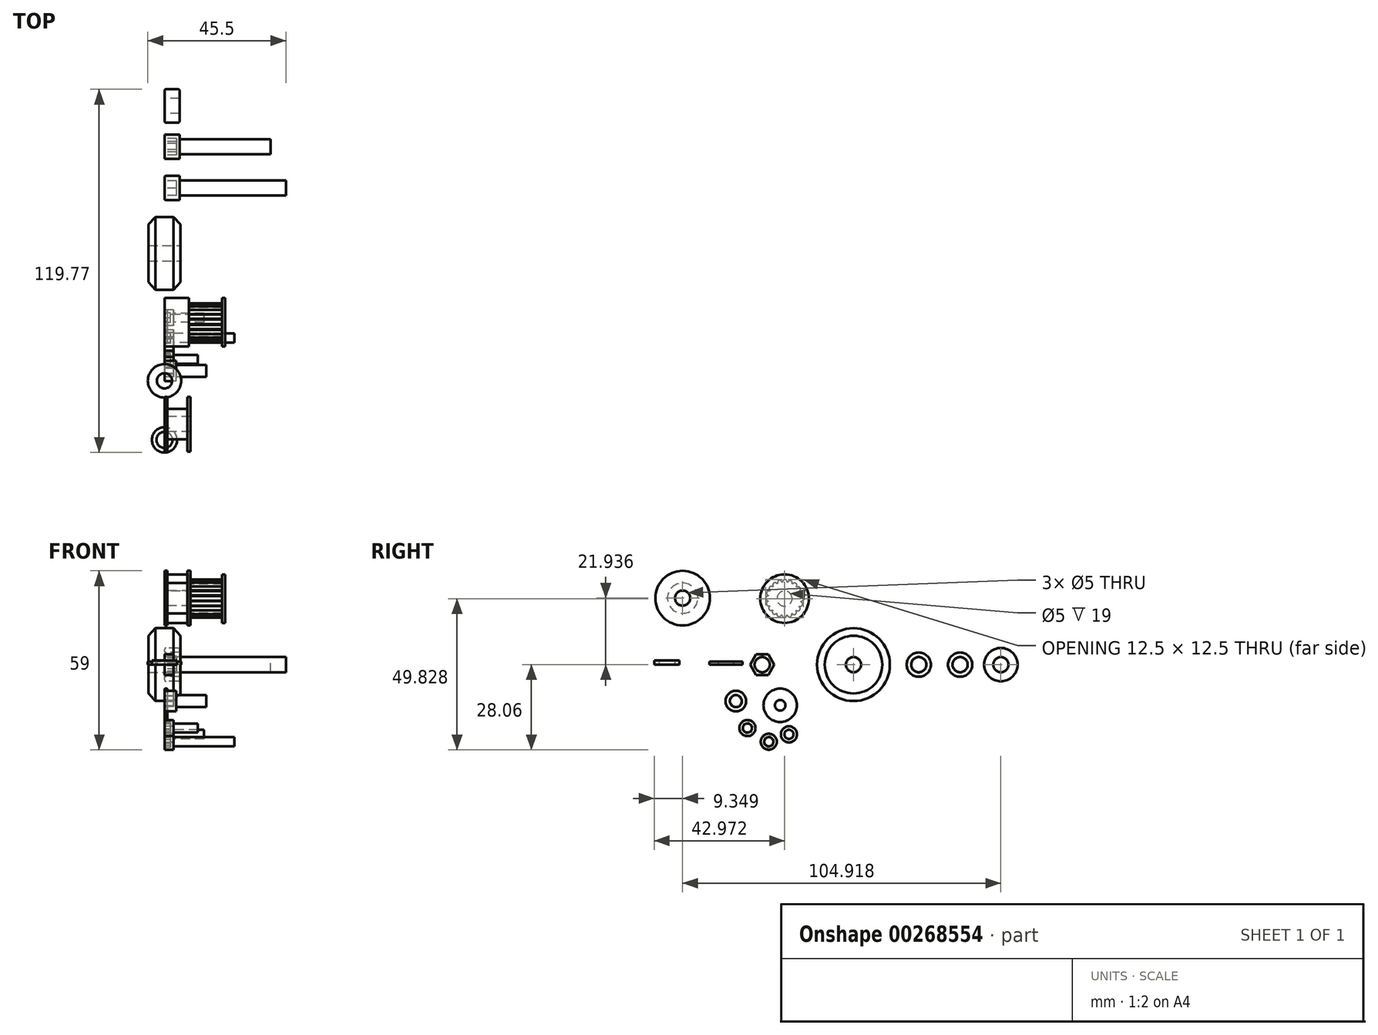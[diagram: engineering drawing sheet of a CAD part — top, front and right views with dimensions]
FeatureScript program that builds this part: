
annotation { "Feature Type Name" : "Feature", "Feature Type Description" : "" }
export const myFeature = defineFeature(function(context is Context, id is Id, definition is map)
    precondition{}
    {
        {
            var Q0;
            Q0=qCreatedBy(makeId("Top.planeOp"),FACE);
            var sketch = newSketch(context, id + "F0", { "sketchPlane" : qUnion([Q0])});
            skLineSegment(sketch, "E0", {"start": v(0, 12) * mm, "end": v(3, 12) * mm});
            skLineSegment(sketch, "E1", {"start": v(3, 12) * mm, "end": v(5.25, 9.5) * mm});
            skLineSegment(sketch, "E2", {"start": v(5.25, 9.5) * mm, "end": v(5.25, 2.5) * mm});
            skPoint(sketch, "E3.end.orphan", {"position": v(2.76, 0) * mm});
            skLineSegment(sketch, "E4", {"start": v(5.25, 2.5) * mm, "end": v(0, 2.5) * mm});
            skLineSegment(sketch, "E5", {"start": v(0, 2.5) * mm, "end": v(0, 12) * mm});
            skLineSegment(sketch, "E6.MirrorCS", {"start": v(0, 12) * mm, "end": v(-3, 12) * mm});
            skLineSegment(sketch, "E7.MirrorCS", {"start": v(-3, 12) * mm, "end": v(-5.25, 9.5) * mm});
            skLineSegment(sketch, "E8.MirrorCS", {"start": v(-5.25, 9.5) * mm, "end": v(-5.25, 2.5) * mm});
            skLineSegment(sketch, "E9.MirrorCS", {"start": v(-5.25, 2.5) * mm, "end": v(0, 2.5) * mm});
            skSolve(sketch);
        }
        {
            var Q0;
            Q0=qCreatedBy(makeId("Front.planeOp"),FACE);
            var sketch = newSketch(context, id + "F1", { "sketchPlane" : qUnion([Q0])});
            skLineSegment(sketch, "E10", {"start": v(9.9, 0) * mm, "end": v(-12.3, 0) * mm, "construction": true});
            skSolve(sketch);
        }
        {
            var Q0;
            Q0 = qSketchRegion(id + "F0", true);
            var Q1;
            Q1=sQuery(id+"F1.wireOp",EDGE,"E10");
            revolve(context, id + "F2", {"entities" : qUnion([Q0]), "axis" : qUnion([Q1]), "revolveType" : RevolveType.FULL});
        }
        {
            var Q0;
            Q0=qCreatedBy(makeId("Right.planeOp"),FACE);
            var sketch = newSketch(context, id + "F3", { "sketchPlane" : qUnion([Q0])});
            skCircle(sketch, "E11", {"center": v(35.14, 0) * mm, "radius": 4 * mm});
            skSolve(sketch);
        }
        {
            var Q0;
            Q0=makeQuery(id+"F3.imprint","IMPRINT",FACE,{"disambiguationData":[TD([[makeQuery(id+"F3.imprint","IMPRINT",EDGE,{"derivedFrom":sQuery(id+"F3.wireOp",EDGE,"E11")}),1.0]])]});
            var Q1;
            Q1=sQuery(id+"F3.wireOp",EDGE,"E11");
            extrude(context, id + "F4", {"entities" : qUnion([Q0]), "surfaceEntities" : qUnion([Q1]), "depth" : 5 * mm});
        }
        {
            var Q0;
            Q0=makeQuery(id+"F4.opExtrude","CAP_FACE",FACE,{"disambiguationData":[OSD([sQuery(id+"F3.wireOp",EDGE,"E11")])],"isStart":false});
            var sketch = newSketch(context, id + "F5", { "sketchPlane" : qUnion([Q0])});
            skCircle(sketch, "E12", {"center": v(35.14, 0) * mm, "radius": 2.5 * mm});
            skSolve(sketch);
        }
        {
            var Q0;
            Q0=makeQuery(id+"F5.imprint","IMPRINT",FACE,{"disambiguationData":[TD([[makeQuery(id+"F5.imprint","IMPRINT",EDGE,{"derivedFrom":sQuery(id+"F5.wireOp",EDGE,"E12")}),1.0]])]});
            extrude(context, id + "F6", {"entities" : qUnion([Q0]), "operationType" : NewBodyOperationType.ADD, "depth" : 30 * mm});
        }
        {
            var Q0;
            Q0=makeQuery(id+"F4.opExtrude","CAP_FACE",FACE,{"disambiguationData":[OSD([sQuery(id+"F3.wireOp",EDGE,"E11")])],"isStart":true});
            var sketch = newSketch(context, id + "F7", { "sketchPlane" : qUnion([Q0])});
            skCircle(sketch, "E13.cCircle", {"center": v(-35.14, 0) * mm, "radius": 2.76 * mm, "construction": true});
            skLineSegment(sketch, "E13.0", {"start": v(-34.13, -2.56) * mm, "end": v(-36.86, -2.16) * mm});
            skLineSegment(sketch, "E13.1", {"start": v(-36.86, -2.16) * mm, "end": v(-37.87, 0.4) * mm});
            skLineSegment(sketch, "E13.2", {"start": v(-37.87, 0.4) * mm, "end": v(-36.16, 2.56) * mm});
            skLineSegment(sketch, "E13.3", {"start": v(-36.16, 2.56) * mm, "end": v(-33.43, 2.16) * mm});
            skLineSegment(sketch, "E13.4", {"start": v(-33.43, 2.16) * mm, "end": v(-32.42, -0.4) * mm});
            skLineSegment(sketch, "E13.5", {"start": v(-32.42, -0.4) * mm, "end": v(-34.13, -2.56) * mm});
            skSolve(sketch);
        }
        {
            var Q0;
            Q0=makeQuery(id+"F7.imprint","IMPRINT",FACE,{"disambiguationData":[TD([[makeQuery(id+"F7.imprint","IMPRINT",EDGE,{"derivedFrom":sQuery(id+"F7.wireOp",EDGE,"E13.0")}),-1.0]])]});
            extrude(context, id + "F8", {"entities" : qUnion([Q0]), "operationType" : NewBodyOperationType.REMOVE, "oppositeDirection" : true, "depth" : 4 * mm});
        }
        {
            var Q0;
            Q0=qCreatedBy(makeId("Right.planeOp"),FACE);
            var sketch = newSketch(context, id + "F9", { "sketchPlane" : qUnion([Q0])});
            skCircle(sketch, "E14", {"center": v(48.59, 0) * mm, "radius": 5.5 * mm});
            skCircle(sketch, "E15", {"center": v(48.59, 0) * mm, "radius": 2.5 * mm});
            skSolve(sketch);
        }
        {
            var Q0;
            Q0 = qSketchRegion(id + "F9", true);
            extrude(context, id + "F10", {"entities" : qUnion([Q0]), "depth" : 5 * mm});
        }
        {
            var Q0;
            Q0=makeQuery(id+"F10.opExtrude","CAP_EDGE",EDGE,{"disambiguationData":[OSD([sQuery(id+"F9.wireOp",EDGE,"E14")])],"isStart":false});
            var Q1;
            Q1=makeQuery(id+"F10.opExtrude","CAP_EDGE",EDGE,{"disambiguationData":[OSD([sQuery(id+"F9.wireOp",EDGE,"E14")])],"isStart":true});
            fillet(context, id + "F11", {"entities" : qUnion([Q0, Q1]), "radius" : .5 * mm, "tangentPropagation" : true, "allowEdgeOverflow" : false});
        }
        {
            var Q0;
            Q0=qCreatedBy(makeId("Right.planeOp"),FACE);
            var sketch = newSketch(context, id + "F12", { "sketchPlane" : qUnion([Q0])});
            skCircle(sketch, "E16.cCircle", {"center": v(-30.1, 0) * mm, "radius": 4 * mm, "construction": true});
            skLineSegment(sketch, "E16.0", {"start": v(-28.07, -3.45) * mm, "end": v(-32.07, -3.48) * mm});
            skLineSegment(sketch, "E16.1", {"start": v(-32.07, -3.48) * mm, "end": v(-34.1, -0.04) * mm});
            skLineSegment(sketch, "E16.2", {"start": v(-34.1, -0.04) * mm, "end": v(-32.13, 3.45) * mm});
            skLineSegment(sketch, "E16.3", {"start": v(-32.13, 3.45) * mm, "end": v(-28.13, 3.48) * mm});
            skLineSegment(sketch, "E16.4", {"start": v(-28.13, 3.48) * mm, "end": v(-26.1, 0.04) * mm});
            skLineSegment(sketch, "E16.5", {"start": v(-26.1, 0.04) * mm, "end": v(-28.07, -3.45) * mm});
            skCircle(sketch, "E17", {"center": v(-30.1, 0) * mm, "radius": 2.5 * mm});
            skSolve(sketch);
        }
        {
            var Q0;
            Q0=makeQuery(id+"F12.imprint","IMPRINT",FACE,{"disambiguationData":[TD([[makeQuery(id+"F12.imprint","IMPRINT",EDGE,{"derivedFrom":sQuery(id+"F12.wireOp",EDGE,"E16.0")}),-1.0]])]});
            extrude(context, id + "F13", {"entities" : qUnion([Q0]), "depth" : 3 * mm});
        }
        {
            var Q0;
            Q0=qCreatedBy(makeId("Top.planeOp"),FACE);
            var sketch = newSketch(context, id + "F14", { "sketchPlane" : qUnion([Q0])});
            skCircle(sketch, "E18", {"center": v(0, -42.06) * mm, "radius": 5.5 * mm});
            skCircle(sketch, "E19", {"center": v(0, -42.06) * mm, "radius": 2.5 * mm});
            skSolve(sketch);
        }
        {
            var Q0;
            Q0=makeQuery(id+"F14.imprint","IMPRINT",FACE,{"disambiguationData":[TD([[makeQuery(id+"F14.imprint","IMPRINT",EDGE,{"derivedFrom":sQuery(id+"F14.wireOp",EDGE,"E18")}),1.0]])]});
            extrude(context, id + "F15", {"entities" : qUnion([Q0]), "depth" : 1 * mm});
        }
        {
            var Q0;
            Q0=qCreatedBy(makeId("Top.planeOp"),FACE);
            var sketch = newSketch(context, id + "F16", { "sketchPlane" : qUnion([Q0])});
            skCircle(sketch, "E20", {"center": v(0, -61.53) * mm, "radius": 4.15 * mm});
            skCircle(sketch, "E21", {"center": v(0, -61.53) * mm, "radius": 2.65 * mm});
            skSolve(sketch);
        }
        {
            var Q0;
            Q0=makeQuery(id+"F16.imprint","IMPRINT",FACE,{"disambiguationData":[TD([[makeQuery(id+"F16.imprint","IMPRINT",EDGE,{"derivedFrom":sQuery(id+"F16.wireOp",EDGE,"E20")}),1.0]])]});
            extrude(context, id + "F17", {"entities" : qUnion([Q0]), "depth" : 1.4 * mm});
        }
        {
            var Q0;
            Q0=qCreatedBy(makeId("Right.planeOp"),FACE);
            var sketch = newSketch(context, id + "F18", { "sketchPlane" : qUnion([Q0])});
            skCircle(sketch, "E22", {"center": v(-38.77, -12.03) * mm, "radius": 3.4 * mm});
            skSolve(sketch);
        }
        {
            var Q0;
            Q0=makeQuery(id+"F18.imprint","IMPRINT",FACE,{"disambiguationData":[TD([[makeQuery(id+"F18.imprint","IMPRINT",EDGE,{"derivedFrom":sQuery(id+"F18.wireOp",EDGE,"E22")}),1.0]])]});
            extrude(context, id + "F19", {"entities" : qUnion([Q0]), "depth" : 3.8 * mm});
        }
        {
            var Q0;
            Q0=makeQuery(id+"F19.opExtrude","CAP_FACE",FACE,{"disambiguationData":[OSD([sQuery(id+"F18.wireOp",EDGE,"E22")])],"isStart":true});
            fillet(context, id + "F20", {"entities" : qUnion([Q0]), "radius" : .5 * mm, "tangentPropagation" : true, "allowEdgeOverflow" : false});
        }
        {
            var Q0;
            Q0=makeQuery(id+"F19.opExtrude","CAP_FACE",FACE,{"disambiguationData":[OSD([sQuery(id+"F18.wireOp",EDGE,"E22")])],"isStart":true});
            var sketch = newSketch(context, id + "F21", { "sketchPlane" : qUnion([Q0])});
            skCircle(sketch, "E23.cCircle", {"center": v(38.77, -12.03) * mm, "radius": 1.7 * mm, "construction": true});
            skLineSegment(sketch, "E23.0", {"start": v(36.82, -11.85) * mm, "end": v(37.95, -10.25) * mm});
            skLineSegment(sketch, "E23.1", {"start": v(37.95, -10.25) * mm, "end": v(39.9, -10.42) * mm});
            skLineSegment(sketch, "E23.2", {"start": v(39.9, -10.42) * mm, "end": v(40.73, -12.2) * mm});
            skLineSegment(sketch, "E23.3", {"start": v(40.73, -12.2) * mm, "end": v(39.6, -13.8) * mm});
            skLineSegment(sketch, "E23.4", {"start": v(39.6, -13.8) * mm, "end": v(37.64, -13.63) * mm});
            skLineSegment(sketch, "E23.5", {"start": v(37.64, -13.63) * mm, "end": v(36.82, -11.85) * mm});
            skPoint(sketch, "E23.0.midPoint", {"position": v(37.38, -11.05) * mm});
            skSolve(sketch);
        }
        {
            var Q0;
            Q0=makeQuery(id+"F21.imprint","IMPRINT",FACE,{"disambiguationData":[TD([[makeQuery(id+"F21.imprint","IMPRINT",EDGE,{"derivedFrom":sQuery(id+"F21.wireOp",EDGE,"E23.0")}),-1.0]])]});
            extrude(context, id + "F22", {"entities" : qUnion([Q0]), "operationType" : NewBodyOperationType.REMOVE, "oppositeDirection" : true, "depth" : 3 * mm});
        }
        {
            var Q0;
            Q0=makeQuery(id+"F19.opExtrude","CAP_FACE",FACE,{"disambiguationData":[OSD([sQuery(id+"F18.wireOp",EDGE,"E22")])],"isStart":false});
            var sketch = newSketch(context, id + "F23", { "sketchPlane" : qUnion([Q0])});
            skCircle(sketch, "E24", {"center": v(-38.77, -12.03) * mm, "radius": 2 * mm});
            skSolve(sketch);
        }
        {
            var Q0;
            Q0=makeQuery(id+"F23.imprint","IMPRINT",FACE,{"disambiguationData":[TD([[makeQuery(id+"F23.imprint","IMPRINT",EDGE,{"derivedFrom":sQuery(id+"F23.wireOp",EDGE,"E24")}),1.0]])]});
            extrude(context, id + "F24", {"entities" : qUnion([Q0]), "operationType" : NewBodyOperationType.ADD, "depth" : 10 * mm});
        }
        {
            var Q0;
            Q0=qCreatedBy(makeId("Right.planeOp"),FACE);
            var sketch = newSketch(context, id + "F25", { "sketchPlane" : qUnion([Q0])});
            skCircle(sketch, "E25", {"center": v(-22.7, 21.77) * mm, "radius": 8 * mm});
            skSolve(sketch);
        }
        {
            var Q0;
            Q0=makeQuery(id+"F25.imprint","IMPRINT",FACE,{"disambiguationData":[TD([[makeQuery(id+"F25.imprint","IMPRINT",EDGE,{"derivedFrom":sQuery(id+"F25.wireOp",EDGE,"E25")}),1.0]])]});
            extrude(context, id + "F26", {"entities" : qUnion([Q0]), "depth" : 20 * mm});
        }
        {
            var Q0;
            Q0=makeQuery(id+"F26.opExtrude","CAP_FACE",FACE,{"disambiguationData":[OSD([sQuery(id+"F25.wireOp",EDGE,"E25")])],"isStart":false});
            cPlane(context, id + "F27", {"entities" : qUnion([Q0]), "cplaneType" : CPlaneType.OFFSET, "offset" : 1 * mm, "oppositeDirection" : true, "width" : 150 * mm, "height" : 150 * mm});
        }
        {
            var Q0;
            Q0=qCreatedBy(id+"F27.planeOp",FACE);
            var sketch = newSketch(context, id + "F28", { "sketchPlane" : qUnion([Q0])});
            skCircle(sketch, "E26", {"center": v(-22.7, 21.77) * mm, "radius": 8.85 * mm});
            skCircle(sketch, "E27", {"center": v(-22.7, 21.77) * mm, "radius": 5.5 * mm});
            skSolve(sketch);
        }
        {
            var Q0;
            Q0=makeQuery(id+"F28.imprint","IMPRINT",FACE,{"disambiguationData":[TD([[makeQuery(id+"F28.imprint","IMPRINT",EDGE,{"derivedFrom":sQuery(id+"F28.wireOp",EDGE,"E26")}),1.0]])]});
            extrude(context, id + "F29", {"entities" : qUnion([Q0]), "operationType" : NewBodyOperationType.REMOVE, "oppositeDirection" : true, "depth" : 11 * mm});
        }
        {
            var Q0;
            Q0=makeQuery(id+"F29.boolean.opBoolean","COPY",FACE,{"derivedFrom":makeQuery(id+"F29.opExtrude","CAP_FACE",FACE,{"disambiguationData":[OSD([sQuery(id+"F28.wireOp",EDGE,"E26"),sQuery(id+"F28.wireOp",EDGE,"E27")])],"isStart":false})});
            var sketch = newSketch(context, id + "F30", { "sketchPlane" : qUnion([Q0])});
            skCircle(sketch, "E28", {"center": v(-28.2, 21.86) * mm, "radius": 0.75 * mm});
            skCircle(sketch, "E29.1.0", {"center": v(-27.97, 20.16) * mm, "radius": 0.75 * mm});
            skCircle(sketch, "E29.2.0", {"center": v(-27.21, 18.61) * mm, "radius": 0.75 * mm});
            skCircle(sketch, "E29.3.0", {"center": v(-26.02, 17.38) * mm, "radius": 0.75 * mm});
            skCircle(sketch, "E29.4.0", {"center": v(-24.5, 16.57) * mm, "radius": 0.75 * mm});
            skCircle(sketch, "E29.5.0", {"center": v(-22.8, 16.27) * mm, "radius": 0.75 * mm});
            skCircle(sketch, "E29.6.0", {"center": v(-21.1, 16.5) * mm, "radius": 0.75 * mm});
            skCircle(sketch, "E29.7.0", {"center": v(-19.55, 17.26) * mm, "radius": 0.75 * mm});
            skCircle(sketch, "E29.8.0", {"center": v(-18.32, 18.46) * mm, "radius": 0.75 * mm});
            skCircle(sketch, "E29.9.0", {"center": v(-17.5, 19.98) * mm, "radius": 0.75 * mm});
            skCircle(sketch, "E29.10.0", {"center": v(-17.2, 21.67) * mm, "radius": 0.75 * mm});
            skCircle(sketch, "E29.11.0", {"center": v(-17.45, 23.38) * mm, "radius": 0.75 * mm});
            skCircle(sketch, "E29.12.0", {"center": v(-18.2, 24.92) * mm, "radius": 0.75 * mm});
            skCircle(sketch, "E29.13.0", {"center": v(-19.4, 26.16) * mm, "radius": 0.75 * mm});
            skCircle(sketch, "E29.14.0", {"center": v(-20.92, 26.97) * mm, "radius": 0.75 * mm});
            skCircle(sketch, "E29.15.0", {"center": v(-22.61, 27.27) * mm, "radius": 0.75 * mm});
            skPoint(sketch, "E29.center", {"position": v(-22.7, 21.77) * mm});
            skCircle(sketch, "E30.1.16.0", {"center": v(-24.32, 27.03) * mm, "radius": 0.75 * mm});
            skCircle(sketch, "E30.1.17.0", {"center": v(-25.86, 26.27) * mm, "radius": 0.75 * mm});
            skCircle(sketch, "E30.1.18.0", {"center": v(-27.1, 25.08) * mm, "radius": 0.75 * mm});
            skCircle(sketch, "E30.1.19.0", {"center": v(-27.9, 23.56) * mm, "radius": 0.75 * mm});
            skSolve(sketch);
        }
        {
            var Q0;
            {var subQ0=sQuery(id+"F30.wireOp",EDGE,"E28");var subQ1=makeQuery(id+"F29.boolean.opBoolean","COPY",EDGE,{"derivedFrom":makeQuery(id+"F29.opExtrude","CAP_EDGE",EDGE,{"disambiguationData":[OSD([sQuery(id+"F28.wireOp",EDGE,"E27")])],"isStart":false})});var subQ2=makeQuery(id+"F30.imprint","INTERSECT",VERTEX,{"disambiguationData":[OD(0.0)],"derivedFrom":[subQ1,subQ0]});Q0=makeQuery(id+"F30.imprint","IMPRINT",FACE,{"disambiguationData":[TD([[makeQuery(id+"F30.imprint","IMPRINT",EDGE,{"disambiguationData":[TD([[subQ2,1.0]])],"derivedFrom":subQ0}),1.0]])]});}
            var Q1;
            {var subQ0=sQuery(id+"F30.wireOp",EDGE,"E30.1.19.0");var subQ1=makeQuery(id+"F29.boolean.opBoolean","COPY",EDGE,{"derivedFrom":makeQuery(id+"F29.opExtrude","CAP_EDGE",EDGE,{"disambiguationData":[OSD([sQuery(id+"F28.wireOp",EDGE,"E27")])],"isStart":false})});var subQ2=makeQuery(id+"F30.imprint","INTERSECT",VERTEX,{"disambiguationData":[OD(0.0)],"derivedFrom":[subQ1,subQ0]});Q1=makeQuery(id+"F30.imprint","IMPRINT",FACE,{"disambiguationData":[TD([[makeQuery(id+"F30.imprint","IMPRINT",EDGE,{"disambiguationData":[TD([[subQ2,1.0]])],"derivedFrom":subQ0}),1.0]])]});}
            var Q2;
            {var subQ0=sQuery(id+"F30.wireOp",EDGE,"E30.1.18.0");var subQ1=makeQuery(id+"F29.boolean.opBoolean","COPY",EDGE,{"derivedFrom":makeQuery(id+"F29.opExtrude","CAP_EDGE",EDGE,{"disambiguationData":[OSD([sQuery(id+"F28.wireOp",EDGE,"E27")])],"isStart":false})});var subQ2=makeQuery(id+"F30.imprint","INTERSECT",VERTEX,{"disambiguationData":[OD(0.0)],"derivedFrom":[subQ1,subQ0]});Q2=makeQuery(id+"F30.imprint","IMPRINT",FACE,{"disambiguationData":[TD([[makeQuery(id+"F30.imprint","IMPRINT",EDGE,{"disambiguationData":[TD([[subQ2,1.0]])],"derivedFrom":subQ0}),1.0]])]});}
            var Q3;
            {var subQ0=sQuery(id+"F30.wireOp",EDGE,"E30.1.17.0");var subQ1=makeQuery(id+"F29.boolean.opBoolean","COPY",EDGE,{"derivedFrom":makeQuery(id+"F29.opExtrude","CAP_EDGE",EDGE,{"disambiguationData":[OSD([sQuery(id+"F28.wireOp",EDGE,"E27")])],"isStart":false})});var subQ2=makeQuery(id+"F30.imprint","INTERSECT",VERTEX,{"disambiguationData":[OD(0.0)],"derivedFrom":[subQ1,subQ0]});Q3=makeQuery(id+"F30.imprint","IMPRINT",FACE,{"disambiguationData":[TD([[makeQuery(id+"F30.imprint","IMPRINT",EDGE,{"disambiguationData":[TD([[subQ2,1.0]])],"derivedFrom":subQ0}),1.0]])]});}
            var Q4;
            {var subQ0=sQuery(id+"F30.wireOp",EDGE,"E30.1.16.0");var subQ1=makeQuery(id+"F29.boolean.opBoolean","COPY",EDGE,{"derivedFrom":makeQuery(id+"F29.opExtrude","CAP_EDGE",EDGE,{"disambiguationData":[OSD([sQuery(id+"F28.wireOp",EDGE,"E27")])],"isStart":false})});var subQ2=makeQuery(id+"F30.imprint","INTERSECT",VERTEX,{"disambiguationData":[OD(0.0)],"derivedFrom":[subQ1,subQ0]});Q4=makeQuery(id+"F30.imprint","IMPRINT",FACE,{"disambiguationData":[TD([[makeQuery(id+"F30.imprint","IMPRINT",EDGE,{"disambiguationData":[TD([[subQ2,1.0]])],"derivedFrom":subQ0}),1.0]])]});}
            var Q5;
            {var subQ0=sQuery(id+"F30.wireOp",EDGE,"E29.15.0");var subQ1=makeQuery(id+"F29.boolean.opBoolean","COPY",EDGE,{"derivedFrom":makeQuery(id+"F29.opExtrude","CAP_EDGE",EDGE,{"disambiguationData":[OSD([sQuery(id+"F28.wireOp",EDGE,"E27")])],"isStart":false})});var subQ2=makeQuery(id+"F30.imprint","INTERSECT",VERTEX,{"disambiguationData":[OD(0.0)],"derivedFrom":[subQ1,subQ0]});Q5=makeQuery(id+"F30.imprint","IMPRINT",FACE,{"disambiguationData":[TD([[makeQuery(id+"F30.imprint","IMPRINT",EDGE,{"disambiguationData":[TD([[subQ2,1.0]])],"derivedFrom":subQ0}),1.0]])]});}
            var Q6;
            {var subQ0=sQuery(id+"F30.wireOp",EDGE,"E29.14.0");var subQ1=makeQuery(id+"F29.boolean.opBoolean","COPY",EDGE,{"derivedFrom":makeQuery(id+"F29.opExtrude","CAP_EDGE",EDGE,{"disambiguationData":[OSD([sQuery(id+"F28.wireOp",EDGE,"E27")])],"isStart":false})});var subQ2=makeQuery(id+"F30.imprint","INTERSECT",VERTEX,{"disambiguationData":[OD(0.0)],"derivedFrom":[subQ1,subQ0]});Q6=makeQuery(id+"F30.imprint","IMPRINT",FACE,{"disambiguationData":[TD([[makeQuery(id+"F30.imprint","IMPRINT",EDGE,{"disambiguationData":[TD([[subQ2,1.0]])],"derivedFrom":subQ0}),1.0]])]});}
            var Q7;
            {var subQ0=sQuery(id+"F30.wireOp",EDGE,"E29.1.0");var subQ1=makeQuery(id+"F29.boolean.opBoolean","COPY",EDGE,{"derivedFrom":makeQuery(id+"F29.opExtrude","CAP_EDGE",EDGE,{"disambiguationData":[OSD([sQuery(id+"F28.wireOp",EDGE,"E27")])],"isStart":false})});var subQ2=makeQuery(id+"F30.imprint","INTERSECT",VERTEX,{"disambiguationData":[OD(0.0)],"derivedFrom":[subQ1,subQ0]});Q7=makeQuery(id+"F30.imprint","IMPRINT",FACE,{"disambiguationData":[TD([[makeQuery(id+"F30.imprint","IMPRINT",EDGE,{"disambiguationData":[TD([[subQ2,1.0]])],"derivedFrom":subQ0}),1.0]])]});}
            var Q8;
            {var subQ0=sQuery(id+"F30.wireOp",EDGE,"E29.2.0");var subQ1=makeQuery(id+"F29.boolean.opBoolean","COPY",EDGE,{"derivedFrom":makeQuery(id+"F29.opExtrude","CAP_EDGE",EDGE,{"disambiguationData":[OSD([sQuery(id+"F28.wireOp",EDGE,"E27")])],"isStart":false})});var subQ2=makeQuery(id+"F30.imprint","INTERSECT",VERTEX,{"disambiguationData":[OD(0.0)],"derivedFrom":[subQ1,subQ0]});Q8=makeQuery(id+"F30.imprint","IMPRINT",FACE,{"disambiguationData":[TD([[makeQuery(id+"F30.imprint","IMPRINT",EDGE,{"disambiguationData":[TD([[subQ2,-1.0]])],"derivedFrom":subQ0}),1.0]])]});}
            var Q9;
            {var subQ0=sQuery(id+"F30.wireOp",EDGE,"E29.3.0");var subQ1=makeQuery(id+"F29.boolean.opBoolean","COPY",EDGE,{"derivedFrom":makeQuery(id+"F29.opExtrude","CAP_EDGE",EDGE,{"disambiguationData":[OSD([sQuery(id+"F28.wireOp",EDGE,"E27")])],"isStart":false})});var subQ2=makeQuery(id+"F30.imprint","INTERSECT",VERTEX,{"disambiguationData":[OD(0.0)],"derivedFrom":[subQ1,subQ0]});Q9=makeQuery(id+"F30.imprint","IMPRINT",FACE,{"disambiguationData":[TD([[makeQuery(id+"F30.imprint","IMPRINT",EDGE,{"disambiguationData":[TD([[subQ2,-1.0]])],"derivedFrom":subQ0}),1.0]])]});}
            var Q10;
            {var subQ0=sQuery(id+"F30.wireOp",EDGE,"E29.4.0");var subQ1=makeQuery(id+"F29.boolean.opBoolean","COPY",EDGE,{"derivedFrom":makeQuery(id+"F29.opExtrude","CAP_EDGE",EDGE,{"disambiguationData":[OSD([sQuery(id+"F28.wireOp",EDGE,"E27")])],"isStart":false})});var subQ2=makeQuery(id+"F30.imprint","INTERSECT",VERTEX,{"disambiguationData":[OD(0.0)],"derivedFrom":[subQ1,subQ0]});Q10=makeQuery(id+"F30.imprint","IMPRINT",FACE,{"disambiguationData":[TD([[makeQuery(id+"F30.imprint","IMPRINT",EDGE,{"disambiguationData":[TD([[subQ2,-1.0]])],"derivedFrom":subQ0}),1.0]])]});}
            var Q11;
            {var subQ0=sQuery(id+"F30.wireOp",EDGE,"E29.5.0");var subQ1=makeQuery(id+"F29.boolean.opBoolean","COPY",EDGE,{"derivedFrom":makeQuery(id+"F29.opExtrude","CAP_EDGE",EDGE,{"disambiguationData":[OSD([sQuery(id+"F28.wireOp",EDGE,"E27")])],"isStart":false})});var subQ2=makeQuery(id+"F30.imprint","INTERSECT",VERTEX,{"disambiguationData":[OD(0.0)],"derivedFrom":[subQ1,subQ0]});Q11=makeQuery(id+"F30.imprint","IMPRINT",FACE,{"disambiguationData":[TD([[makeQuery(id+"F30.imprint","IMPRINT",EDGE,{"disambiguationData":[TD([[subQ2,-1.0]])],"derivedFrom":subQ0}),1.0]])]});}
            var Q12;
            {var subQ0=sQuery(id+"F30.wireOp",EDGE,"E29.7.0");var subQ1=makeQuery(id+"F29.boolean.opBoolean","COPY",EDGE,{"derivedFrom":makeQuery(id+"F29.opExtrude","CAP_EDGE",EDGE,{"disambiguationData":[OSD([sQuery(id+"F28.wireOp",EDGE,"E27")])],"isStart":false})});var subQ2=makeQuery(id+"F30.imprint","INTERSECT",VERTEX,{"disambiguationData":[OD(0.0)],"derivedFrom":[subQ1,subQ0]});Q12=makeQuery(id+"F30.imprint","IMPRINT",FACE,{"disambiguationData":[TD([[makeQuery(id+"F30.imprint","IMPRINT",EDGE,{"disambiguationData":[TD([[subQ2,-1.0]])],"derivedFrom":subQ0}),1.0]])]});}
            var Q13;
            {var subQ0=sQuery(id+"F30.wireOp",EDGE,"E29.6.0");var subQ1=makeQuery(id+"F29.boolean.opBoolean","COPY",EDGE,{"derivedFrom":makeQuery(id+"F29.opExtrude","CAP_EDGE",EDGE,{"disambiguationData":[OSD([sQuery(id+"F28.wireOp",EDGE,"E27")])],"isStart":false})});var subQ2=makeQuery(id+"F30.imprint","INTERSECT",VERTEX,{"disambiguationData":[OD(0.0)],"derivedFrom":[subQ1,subQ0]});Q13=makeQuery(id+"F30.imprint","IMPRINT",FACE,{"disambiguationData":[TD([[makeQuery(id+"F30.imprint","IMPRINT",EDGE,{"disambiguationData":[TD([[subQ2,-1.0]])],"derivedFrom":subQ0}),1.0]])]});}
            var Q14;
            {var subQ0=sQuery(id+"F30.wireOp",EDGE,"E29.8.0");var subQ1=makeQuery(id+"F29.boolean.opBoolean","COPY",EDGE,{"derivedFrom":makeQuery(id+"F29.opExtrude","CAP_EDGE",EDGE,{"disambiguationData":[OSD([sQuery(id+"F28.wireOp",EDGE,"E27")])],"isStart":false})});var subQ2=makeQuery(id+"F30.imprint","INTERSECT",VERTEX,{"disambiguationData":[OD(0.0)],"derivedFrom":[subQ1,subQ0]});Q14=makeQuery(id+"F30.imprint","IMPRINT",FACE,{"disambiguationData":[TD([[makeQuery(id+"F30.imprint","IMPRINT",EDGE,{"disambiguationData":[TD([[subQ2,-1.0]])],"derivedFrom":subQ0}),1.0]])]});}
            var Q15;
            {var subQ0=sQuery(id+"F30.wireOp",EDGE,"E29.9.0");var subQ1=makeQuery(id+"F29.boolean.opBoolean","COPY",EDGE,{"derivedFrom":makeQuery(id+"F29.opExtrude","CAP_EDGE",EDGE,{"disambiguationData":[OSD([sQuery(id+"F28.wireOp",EDGE,"E27")])],"isStart":false})});var subQ2=makeQuery(id+"F30.imprint","INTERSECT",VERTEX,{"disambiguationData":[OD(0.0)],"derivedFrom":[subQ1,subQ0]});Q15=makeQuery(id+"F30.imprint","IMPRINT",FACE,{"disambiguationData":[TD([[makeQuery(id+"F30.imprint","IMPRINT",EDGE,{"disambiguationData":[TD([[subQ2,-1.0]])],"derivedFrom":subQ0}),1.0]])]});}
            var Q16;
            {var subQ0=sQuery(id+"F30.wireOp",EDGE,"E29.10.0");var subQ1=makeQuery(id+"F29.boolean.opBoolean","COPY",EDGE,{"derivedFrom":makeQuery(id+"F29.opExtrude","CAP_EDGE",EDGE,{"disambiguationData":[OSD([sQuery(id+"F28.wireOp",EDGE,"E27")])],"isStart":false})});var subQ2=makeQuery(id+"F30.imprint","INTERSECT",VERTEX,{"disambiguationData":[OD(0.0)],"derivedFrom":[subQ1,subQ0]});Q16=makeQuery(id+"F30.imprint","IMPRINT",FACE,{"disambiguationData":[TD([[makeQuery(id+"F30.imprint","IMPRINT",EDGE,{"disambiguationData":[TD([[subQ2,-1.0]])],"derivedFrom":subQ0}),1.0]])]});}
            var Q17;
            {var subQ0=sQuery(id+"F30.wireOp",EDGE,"E29.11.0");var subQ1=makeQuery(id+"F29.boolean.opBoolean","COPY",EDGE,{"derivedFrom":makeQuery(id+"F29.opExtrude","CAP_EDGE",EDGE,{"disambiguationData":[OSD([sQuery(id+"F28.wireOp",EDGE,"E27")])],"isStart":false})});var subQ2=makeQuery(id+"F30.imprint","INTERSECT",VERTEX,{"disambiguationData":[OD(0.0)],"derivedFrom":[subQ1,subQ0]});Q17=makeQuery(id+"F30.imprint","IMPRINT",FACE,{"disambiguationData":[TD([[makeQuery(id+"F30.imprint","IMPRINT",EDGE,{"disambiguationData":[TD([[subQ2,-1.0]])],"derivedFrom":subQ0}),1.0]])]});}
            var Q18;
            {var subQ0=sQuery(id+"F30.wireOp",EDGE,"E29.12.0");var subQ1=makeQuery(id+"F29.boolean.opBoolean","COPY",EDGE,{"derivedFrom":makeQuery(id+"F29.opExtrude","CAP_EDGE",EDGE,{"disambiguationData":[OSD([sQuery(id+"F28.wireOp",EDGE,"E27")])],"isStart":false})});var subQ2=makeQuery(id+"F30.imprint","INTERSECT",VERTEX,{"disambiguationData":[OD(0.0)],"derivedFrom":[subQ1,subQ0]});Q18=makeQuery(id+"F30.imprint","IMPRINT",FACE,{"disambiguationData":[TD([[makeQuery(id+"F30.imprint","IMPRINT",EDGE,{"disambiguationData":[TD([[subQ2,1.0]])],"derivedFrom":subQ0}),1.0]])]});}
            var Q19;
            {var subQ0=sQuery(id+"F30.wireOp",EDGE,"E29.13.0");var subQ1=makeQuery(id+"F29.boolean.opBoolean","COPY",EDGE,{"derivedFrom":makeQuery(id+"F29.opExtrude","CAP_EDGE",EDGE,{"disambiguationData":[OSD([sQuery(id+"F28.wireOp",EDGE,"E27")])],"isStart":false})});var subQ2=makeQuery(id+"F30.imprint","INTERSECT",VERTEX,{"disambiguationData":[OD(0.0)],"derivedFrom":[subQ1,subQ0]});Q19=makeQuery(id+"F30.imprint","IMPRINT",FACE,{"disambiguationData":[TD([[makeQuery(id+"F30.imprint","IMPRINT",EDGE,{"disambiguationData":[TD([[subQ2,1.0]])],"derivedFrom":subQ0}),1.0]])]});}
            var Q20;
            Q20=sQuery(id+"F30.wireOp",EDGE,"E28");
            extrude(context, id + "F31", {"entities" : qUnion([Q0, Q1, Q2, Q3, Q4, Q5, Q6, Q7, Q8, Q9, Q10, Q11, Q12, Q13, Q14, Q15, Q16, Q17, Q18, Q19]), "operationType" : NewBodyOperationType.ADD, "surfaceEntities" : qUnion([Q20]), "endBound" : BoundingType.UP_TO_NEXT, "depth" : 25 * mm});
        }
        {
            var Q0;
            Q0=makeQuery(id+"F26.opExtrude","CAP_FACE",FACE,{"disambiguationData":[OSD([sQuery(id+"F25.wireOp",EDGE,"E25")])],"isStart":true});
            var sketch = newSketch(context, id + "F32", { "sketchPlane" : qUnion([Q0])});
            skCircle(sketch, "E31", {"center": v(22.7, 21.77) * mm, "radius": 2.5 * mm});
            skSolve(sketch);
        }
        {
            var Q0;
            Q0=makeQuery(id+"F32.imprint","IMPRINT",FACE,{"disambiguationData":[TD([[makeQuery(id+"F32.imprint","IMPRINT",EDGE,{"derivedFrom":sQuery(id+"F32.wireOp",EDGE,"E31")}),1.0]])]});
            extrude(context, id + "F33", {"entities" : qUnion([Q0]), "operationType" : NewBodyOperationType.REMOVE, "oppositeDirection" : true, "depth" : 19 * mm});
        }
        {
            var Q0;
            Q0=qCreatedBy(makeId("Right.planeOp"),FACE);
            var sketch = newSketch(context, id + "F34", { "sketchPlane" : qUnion([Q0])});
            skCircle(sketch, "E32", {"center": v(21.52, 0) * mm, "radius": 4 * mm});
            skSolve(sketch);
        }
        {
            var Q0;
            Q0 = qSketchRegion(id + "F34", true);
            extrude(context, id + "F35", {"entities" : qUnion([Q0]), "depth" : 5 * mm});
        }
        {
            var Q0;
            Q0=makeQuery(id+"F35.opExtrude","CAP_FACE",FACE,{"disambiguationData":[OSD([sQuery(id+"F34.wireOp",EDGE,"E32")])],"isStart":false});
            var sketch = newSketch(context, id + "F36", { "sketchPlane" : qUnion([Q0])});
            skCircle(sketch, "E33", {"center": v(21.52, 0) * mm, "radius": 2.5 * mm});
            skSolve(sketch);
        }
        {
            var Q0;
            Q0=makeQuery(id+"F36.imprint","IMPRINT",FACE,{"disambiguationData":[TD([[makeQuery(id+"F36.imprint","IMPRINT",EDGE,{"derivedFrom":sQuery(id+"F36.wireOp",EDGE,"E33")}),1.0]])]});
            extrude(context, id + "F37", {"entities" : qUnion([Q0]), "operationType" : NewBodyOperationType.ADD, "depth" : 35 * mm});
        }
        {
            var Q0;
            Q0=makeQuery(id+"F35.opExtrude","CAP_EDGE",EDGE,{"disambiguationData":[OSD([sQuery(id+"F34.wireOp",EDGE,"E32")])],"isStart":true});
            fillet(context, id + "F38", {"entities" : qUnion([Q0]), "radius" : .5 * mm, "tangentPropagation" : true, "allowEdgeOverflow" : false});
        }
        {
            var Q0;
            Q0=makeQuery(id+"F35.opExtrude","CAP_FACE",FACE,{"disambiguationData":[OSD([sQuery(id+"F34.wireOp",EDGE,"E32")])],"isStart":true});
            var sketch = newSketch(context, id + "F39", { "sketchPlane" : qUnion([Q0])});
            skCircle(sketch, "E34.cCircle", {"center": v(-21.52, 0) * mm, "radius": 2.41 * mm, "construction": true});
            skLineSegment(sketch, "E34.0", {"start": v(-23.94, -1.4) * mm, "end": v(-23.94, 1.4) * mm});
            skLineSegment(sketch, "E34.1", {"start": v(-23.94, 1.4) * mm, "end": v(-21.52, 2.79) * mm});
            skLineSegment(sketch, "E34.2", {"start": v(-21.52, 2.79) * mm, "end": v(-19.11, 1.4) * mm});
            skLineSegment(sketch, "E34.3", {"start": v(-19.11, 1.4) * mm, "end": v(-19.11, -1.4) * mm});
            skLineSegment(sketch, "E34.4", {"start": v(-19.11, -1.4) * mm, "end": v(-21.52, -2.79) * mm});
            skLineSegment(sketch, "E34.5", {"start": v(-21.52, -2.79) * mm, "end": v(-23.94, -1.4) * mm});
            skPoint(sketch, "E34.0.midPoint", {"position": v(-23.94, 0) * mm});
            skSolve(sketch);
        }
        {
            var Q0;
            Q0=makeQuery(id+"F39.imprint","IMPRINT",FACE,{"disambiguationData":[TD([[makeQuery(id+"F39.imprint","IMPRINT",EDGE,{"derivedFrom":sQuery(id+"F39.wireOp",EDGE,"E34.0")}),-1.0]])]});
            extrude(context, id + "F40", {"entities" : qUnion([Q0]), "operationType" : NewBodyOperationType.REMOVE, "oppositeDirection" : true, "depth" : 4 * mm});
        }
        {
            var Q0;
            Q0=qCreatedBy(makeId("Right.planeOp"),FACE);
            var sketch = newSketch(context, id + "F41", { "sketchPlane" : qUnion([Q0])});
            skCircle(sketch, "E35", {"center": v(-56.33, 21.94) * mm, "radius": 9 * mm});
            skCircle(sketch, "E36", {"center": v(-56.33, 21.94) * mm, "radius": 2.5 * mm});
            skSolve(sketch);
        }
        {
            var Q0;
            Q0=makeQuery(id+"F41.imprint","IMPRINT",FACE,{"disambiguationData":[TD([[makeQuery(id+"F41.imprint","IMPRINT",EDGE,{"derivedFrom":sQuery(id+"F41.wireOp",EDGE,"E35")}),1.0]])]});
            extrude(context, id + "F42", {"entities" : qUnion([Q0]), "depth" : 8.6 * mm});
        }
        {
            var Q0;
            Q0=makeQuery(id+"F42.opExtrude","CAP_FACE",FACE,{"disambiguationData":[OSD([sQuery(id+"F41.wireOp",EDGE,"E35"),sQuery(id+"F41.wireOp",EDGE,"E36")])],"isStart":false});
            cPlane(context, id + "F43", {"entities" : qUnion([Q0]), "cplaneType" : CPlaneType.OFFSET, "offset" : 1 * mm, "oppositeDirection" : true, "width" : 150 * mm, "height" : 150 * mm});
        }
        {
            var Q0;
            Q0=qCreatedBy(id+"F43.planeOp",FACE);
            var sketch = newSketch(context, id + "F44", { "sketchPlane" : qUnion([Q0])});
            skCircle(sketch, "E37", {"center": v(-56.33, 21.94) * mm, "radius": 5 * mm});
            skCircle(sketch, "E38", {"center": v(-56.33, 21.94) * mm, "radius": 10.26 * mm});
            skSolve(sketch);
        }
        {
            var Q0;
            Q0=makeQuery(id+"F44.imprint","IMPRINT",FACE,{"disambiguationData":[TD([[makeQuery(id+"F44.imprint","IMPRINT",EDGE,{"derivedFrom":sQuery(id+"F44.wireOp",EDGE,"E37")}),-1.0]])]});
            extrude(context, id + "F45", {"entities" : qUnion([Q0]), "operationType" : NewBodyOperationType.REMOVE, "oppositeDirection" : true, "depth" : 6.6 * mm});
        }
        {
            var Q0;
            Q0=qCreatedBy(makeId("Right.planeOp"),FACE);
            var sketch = newSketch(context, id + "F46", { "sketchPlane" : qUnion([Q0])});
            skCircle(sketch, "E39", {"center": v(-21.28, -22.98) * mm, "radius": 2.65 * mm});
            skSolve(sketch);
        }
        {
            var Q0;
            Q0=makeQuery(id+"F46.imprint","IMPRINT",FACE,{"disambiguationData":[TD([[makeQuery(id+"F46.imprint","IMPRINT",EDGE,{"derivedFrom":sQuery(id+"F46.wireOp",EDGE,"E39")}),1.0]])]});
            var Q1;
            Q1=sQuery(id+"F46.wireOp",EDGE,"E39");
            extrude(context, id + "F47", {"entities" : qUnion([Q0]), "surfaceEntities" : qUnion([Q1]), "depth" : 3 * mm});
        }
        {
            var Q0;
            Q0=makeQuery(id+"F47.opExtrude","CAP_FACE",FACE,{"disambiguationData":[OSD([sQuery(id+"F46.wireOp",EDGE,"E39")])],"isStart":false});
            var sketch = newSketch(context, id + "F48", { "sketchPlane" : qUnion([Q0])});
            skCircle(sketch, "E40", {"center": v(-21.28, -22.98) * mm, "radius": 1.5 * mm});
            skSolve(sketch);
        }
        {
            var Q0;
            Q0=makeQuery(id+"F48.imprint","IMPRINT",FACE,{"disambiguationData":[TD([[makeQuery(id+"F48.imprint","IMPRINT",EDGE,{"derivedFrom":sQuery(id+"F48.wireOp",EDGE,"E40")}),1.0]])]});
            extrude(context, id + "F49", {"entities" : qUnion([Q0]), "operationType" : NewBodyOperationType.ADD, "depth" : 10 * mm});
        }
        {
            var Q0;
            Q0=makeQuery(id+"F47.opExtrude","CAP_FACE",FACE,{"disambiguationData":[OSD([sQuery(id+"F46.wireOp",EDGE,"E39")])],"isStart":true});
            var sketch = newSketch(context, id + "F50", { "sketchPlane" : qUnion([Q0])});
            skCircle(sketch, "E41.cCircle", {"center": v(21.28, -22.98) * mm, "radius": 1.55 * mm, "construction": true});
            skLineSegment(sketch, "E41.0", {"start": v(19.73, -23.88) * mm, "end": v(19.73, -22.1) * mm});
            skLineSegment(sketch, "E41.1", {"start": v(19.73, -22.1) * mm, "end": v(21.28, -21.2) * mm});
            skLineSegment(sketch, "E41.2", {"start": v(21.28, -21.2) * mm, "end": v(22.82, -22.1) * mm});
            skLineSegment(sketch, "E41.3", {"start": v(22.82, -22.1) * mm, "end": v(22.82, -23.88) * mm});
            skLineSegment(sketch, "E41.4", {"start": v(22.82, -23.88) * mm, "end": v(21.28, -24.77) * mm});
            skLineSegment(sketch, "E41.5", {"start": v(21.28, -24.77) * mm, "end": v(19.73, -23.88) * mm});
            skPoint(sketch, "E41.0.midPoint", {"position": v(19.73, -22.98) * mm});
            skSolve(sketch);
        }
        {
            var Q0;
            Q0=makeQuery(id+"F50.imprint","IMPRINT",FACE,{"disambiguationData":[TD([[makeQuery(id+"F50.imprint","IMPRINT",EDGE,{"derivedFrom":sQuery(id+"F50.wireOp",EDGE,"E41.0")}),-1.0]])]});
            extrude(context, id + "F51", {"entities" : qUnion([Q0]), "operationType" : NewBodyOperationType.REMOVE, "oppositeDirection" : true, "depth" : 2 * mm});
        }
        {
            var Q0;
            Q0=qCreatedBy(makeId("Right.planeOp"),FACE);
            var sketch = newSketch(context, id + "F52", { "sketchPlane" : qUnion([Q0])});
            skCircle(sketch, "E42", {"center": v(-34.96, -20.91) * mm, "radius": 2.65 * mm});
            skSolve(sketch);
        }
        {
            var Q0;
            Q0=makeQuery(id+"F52.imprint","IMPRINT",FACE,{"disambiguationData":[TD([[makeQuery(id+"F52.imprint","IMPRINT",EDGE,{"derivedFrom":sQuery(id+"F52.wireOp",EDGE,"E42")}),1.0]])]});
            var Q1;
            Q1=sQuery(id+"F52.wireOp",EDGE,"E42");
            extrude(context, id + "F53", {"entities" : qUnion([Q0]), "surfaceEntities" : qUnion([Q1]), "depth" : 3 * mm});
        }
        {
            var Q0;
            Q0=makeQuery(id+"F53.opExtrude","CAP_FACE",FACE,{"disambiguationData":[OSD([sQuery(id+"F52.wireOp",EDGE,"E42")])],"isStart":false});
            var sketch = newSketch(context, id + "F54", { "sketchPlane" : qUnion([Q0])});
            skCircle(sketch, "E43", {"center": v(-34.96, -20.91) * mm, "radius": 1.5 * mm});
            skSolve(sketch);
        }
        {
            var Q0;
            Q0=makeQuery(id+"F54.imprint","IMPRINT",FACE,{"disambiguationData":[TD([[makeQuery(id+"F54.imprint","IMPRINT",EDGE,{"derivedFrom":sQuery(id+"F54.wireOp",EDGE,"E43")}),1.0]])]});
            extrude(context, id + "F55", {"entities" : qUnion([Q0]), "operationType" : NewBodyOperationType.ADD, "depth" : 8 * mm});
        }
        {
            var Q0;
            Q0=makeQuery(id+"F53.opExtrude","CAP_FACE",FACE,{"disambiguationData":[OSD([sQuery(id+"F52.wireOp",EDGE,"E42")])],"isStart":true});
            var sketch = newSketch(context, id + "F56", { "sketchPlane" : qUnion([Q0])});
            skCircle(sketch, "E44.cCircle", {"center": v(34.96, -20.91) * mm, "radius": 1.68 * mm, "construction": true});
            skLineSegment(sketch, "E44.0", {"start": v(33.1, -20.36) * mm, "end": v(34.5, -19.03) * mm});
            skLineSegment(sketch, "E44.1", {"start": v(34.5, -19.03) * mm, "end": v(36.36, -19.58) * mm});
            skLineSegment(sketch, "E44.2", {"start": v(36.36, -19.58) * mm, "end": v(36.82, -21.46) * mm});
            skLineSegment(sketch, "E44.3", {"start": v(36.82, -21.46) * mm, "end": v(35.4, -22.8) * mm});
            skLineSegment(sketch, "E44.4", {"start": v(35.4, -22.8) * mm, "end": v(33.55, -22.24) * mm});
            skLineSegment(sketch, "E44.5", {"start": v(33.55, -22.24) * mm, "end": v(33.1, -20.36) * mm});
            skPoint(sketch, "E44.0.midPoint", {"position": v(33.8, -19.7) * mm});
            skSolve(sketch);
        }
        {
            var Q0;
            Q0=makeQuery(id+"F56.imprint","IMPRINT",FACE,{"disambiguationData":[TD([[makeQuery(id+"F56.imprint","IMPRINT",EDGE,{"derivedFrom":sQuery(id+"F56.wireOp",EDGE,"E44.0")}),-1.0]])]});
            extrude(context, id + "F57", {"entities" : qUnion([Q0]), "operationType" : NewBodyOperationType.REMOVE, "oppositeDirection" : true, "depth" : 2 * mm});
        }
        {
            var Q0;
            Q0=qCreatedBy(makeId("Right.planeOp"),FACE);
            var sketch = newSketch(context, id + "F58", { "sketchPlane" : qUnion([Q0])});
            skCircle(sketch, "E45", {"center": v(-27.92, -25.4) * mm, "radius": 2.65 * mm});
            skSolve(sketch);
        }
        {
            var Q0;
            Q0=makeQuery(id+"F58.imprint","IMPRINT",FACE,{"disambiguationData":[TD([[makeQuery(id+"F58.imprint","IMPRINT",EDGE,{"derivedFrom":sQuery(id+"F58.wireOp",EDGE,"E45")}),1.0]])]});
            extrude(context, id + "F59", {"entities" : qUnion([Q0]), "depth" : 3 * mm});
        }
        {
            var Q0;
            Q0=makeQuery(id+"F59.opExtrude","CAP_FACE",FACE,{"disambiguationData":[OSD([sQuery(id+"F58.wireOp",EDGE,"E45")])],"isStart":false});
            var sketch = newSketch(context, id + "F60", { "sketchPlane" : qUnion([Q0])});
            skCircle(sketch, "E46", {"center": v(-27.92, -25.4) * mm, "radius": 1.5 * mm});
            skSolve(sketch);
        }
        {
            var Q0;
            Q0=makeQuery(id+"F60.imprint","IMPRINT",FACE,{"disambiguationData":[TD([[makeQuery(id+"F60.imprint","IMPRINT",EDGE,{"derivedFrom":sQuery(id+"F60.wireOp",EDGE,"E46")}),1.0]])]});
            extrude(context, id + "F61", {"entities" : qUnion([Q0]), "operationType" : NewBodyOperationType.ADD, "depth" : 20 * mm});
        }
        {
            var Q0;
            Q0=makeQuery(id+"F59.opExtrude","CAP_FACE",FACE,{"disambiguationData":[OSD([sQuery(id+"F58.wireOp",EDGE,"E45")])],"isStart":true});
            var sketch = newSketch(context, id + "F62", { "sketchPlane" : qUnion([Q0])});
            skCircle(sketch, "E47.cCircle", {"center": v(27.92, -25.4) * mm, "radius": 1.68 * mm, "construction": true});
            skLineSegment(sketch, "E47.0", {"start": v(27.6, -23.5) * mm, "end": v(29.41, -24.17) * mm});
            skLineSegment(sketch, "E47.1", {"start": v(29.41, -24.17) * mm, "end": v(29.74, -26.08) * mm});
            skLineSegment(sketch, "E47.2", {"start": v(29.74, -26.08) * mm, "end": v(28.25, -27.32) * mm});
            skLineSegment(sketch, "E47.3", {"start": v(28.25, -27.32) * mm, "end": v(26.43, -26.65) * mm});
            skLineSegment(sketch, "E47.4", {"start": v(26.43, -26.65) * mm, "end": v(26.1, -24.74) * mm});
            skLineSegment(sketch, "E47.5", {"start": v(26.1, -24.74) * mm, "end": v(27.6, -23.5) * mm});
            skPoint(sketch, "E47.0.midPoint", {"position": v(28.5, -23.83) * mm});
            skSolve(sketch);
        }
        {
            var Q0;
            Q0=makeQuery(id+"F62.imprint","IMPRINT",FACE,{"disambiguationData":[TD([[makeQuery(id+"F62.imprint","IMPRINT",EDGE,{"derivedFrom":sQuery(id+"F62.wireOp",EDGE,"E47.0")}),-1.0]])]});
            extrude(context, id + "F63", {"entities" : qUnion([Q0]), "operationType" : NewBodyOperationType.REMOVE, "oppositeDirection" : true, "depth" : 2 * mm});
        }
        {
            var Q0;
            Q0=qCreatedBy(makeId("Right.planeOp"),FACE);
            var sketch = newSketch(context, id + "F64", { "sketchPlane" : qUnion([Q0])});
            skCircle(sketch, "E48", {"center": v(-24.16, -13.4) * mm, "radius": 5.5 * mm});
            skCircle(sketch, "E49", {"center": v(-24.16, -13.4) * mm, "radius": 1.75 * mm});
            skSolve(sketch);
        }
        {
            var Q0;
            Q0=makeQuery(id+"F64.imprint","IMPRINT",FACE,{"disambiguationData":[TD([[makeQuery(id+"F64.imprint","IMPRINT",EDGE,{"derivedFrom":sQuery(id+"F64.wireOp",EDGE,"E48")}),1.0]])]});
            extrude(context, id + "F65", {"entities" : qUnion([Q0]), "depth" : 1 * mm});
        }
        {
            var Q0;
            Q0=makeQuery(id+"F65.opExtrude","CAP_EDGE",EDGE,{"disambiguationData":[OSD([sQuery(id+"F64.wireOp",EDGE,"E48")])],"isStart":false});
            var Q1;
            Q1=makeQuery(id+"F65.opExtrude","CAP_EDGE",EDGE,{"disambiguationData":[OSD([sQuery(id+"F64.wireOp",EDGE,"E49")])],"isStart":false});
            var Q2;
            Q2=makeQuery(id+"F65.opExtrude","CAP_EDGE",EDGE,{"disambiguationData":[OSD([sQuery(id+"F64.wireOp",EDGE,"E49")])],"isStart":true});
            var Q3;
            Q3=makeQuery(id+"F65.opExtrude","CAP_EDGE",EDGE,{"disambiguationData":[OSD([sQuery(id+"F64.wireOp",EDGE,"E48")])],"isStart":true});
            fillet(context, id + "F66", {"entities" : qUnion([Q0, Q1, Q2, Q3]), "radius" : .3 * mm, "tangentPropagation" : true, "allowEdgeOverflow" : false});
        }
    });
